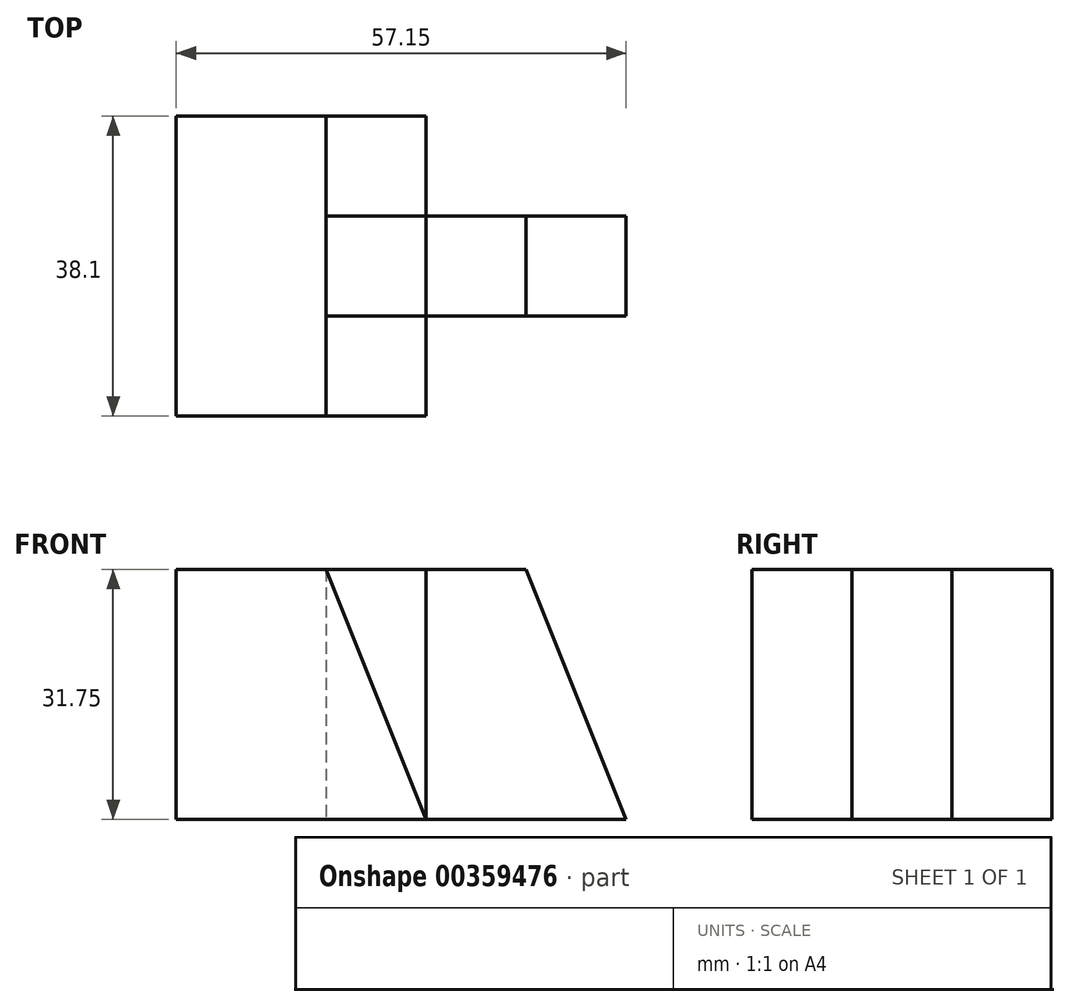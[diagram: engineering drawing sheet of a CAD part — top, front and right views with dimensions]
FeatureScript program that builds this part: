
annotation { "Feature Type Name" : "Feature", "Feature Type Description" : "" }
export const myFeature = defineFeature(function(context is Context, id is Id, definition is map)
    precondition{}
    {
        {
            var Q0;
            Q0=qCreatedBy(makeId("Front.planeOp"),FACE);
            var sketch = newSketch(context, id + "F0", { "sketchPlane" : qUnion([Q0])});
            skLineSegment(sketch, "E0", {"start": v(0, 31.75) * mm, "end": v(0, 0) * mm});
            skLineSegment(sketch, "E1", {"start": v(0, 0) * mm, "end": v(31.75, 0) * mm});
            skLineSegment(sketch, "E2", {"start": v(31.75, 0) * mm, "end": v(31.75, 31.75) * mm});
            skLineSegment(sketch, "E3", {"start": v(31.75, 31.75) * mm, "end": v(0, 31.75) * mm});
            skSolve(sketch);
        }
        {
            var Q0;
            Q0=makeQuery(id+"F0.imprint","IMPRINT",FACE,{"disambiguationData":[TD([[makeQuery(id+"F0.imprint","IMPRINT",EDGE,{"derivedFrom":sQuery(id+"F0.wireOp",EDGE,"E0")}),1.0]])]});
            extrude(context, id + "F1", {"entities" : qUnion([Q0]), "oppositeDirection" : true, "depth" : 38.1 * mm});
        }
        {
            var Q0;
            Q0=qCreatedBy(makeId("Right.planeOp"),FACE);
            var sketch = newSketch(context, id + "F2", { "sketchPlane" : qUnion([Q0])});
            skLineSegment(sketch, "E4", {"start": v(12.7, 31.75) * mm, "end": v(12.7, 0) * mm});
            skLineSegment(sketch, "E5", {"start": v(12.7, 0) * mm, "end": v(25.4, 0) * mm});
            skLineSegment(sketch, "E6", {"start": v(25.4, 0) * mm, "end": v(25.4, 31.75) * mm});
            skLineSegment(sketch, "E7", {"start": v(12.7, 31.75) * mm, "end": v(25.4, 31.75) * mm});
            skSolve(sketch);
        }
        {
            var Q0;
            Q0 = qSketchRegion(id + "F2", true);
            extrude(context, id + "F3", {"entities" : qUnion([Q0]), "operationType" : NewBodyOperationType.ADD, "depth" : 57.15 * mm});
        }
        {
            var Q0;
            Q0=qCreatedBy(makeId("Front.planeOp"),FACE);
            var sketch = newSketch(context, id + "F4", { "sketchPlane" : qUnion([Q0])});
            skLineSegment(sketch, "E8", {"start": v(44.45, 31.75) * mm, "end": v(57.15, 0) * mm});
            skLineSegment(sketch, "E9", {"start": v(57.15, 0) * mm, "end": v(57.15, 31.75) * mm});
            skLineSegment(sketch, "E10", {"start": v(57.15, 31.75) * mm, "end": v(44.45, 31.75) * mm});
            skSolve(sketch);
        }
        {
            var Q0;
            Q0 = qSketchRegion(id + "F4", true);
            extrude(context, id + "F5", {"entities" : qUnion([Q0]), "operationType" : NewBodyOperationType.REMOVE, "oppositeDirection" : true, "depth" : 25.4 * mm});
        }
        {
            var Q0;
            Q0=qCreatedBy(makeId("Front.planeOp"),FACE);
            var sketch = newSketch(context, id + "F6", { "sketchPlane" : qUnion([Q0])});
            skLineSegment(sketch, "E11", {"start": v(19.05, 31.75) * mm, "end": v(31.75, 0) * mm});
            skLineSegment(sketch, "E12", {"start": v(31.75, 0) * mm, "end": v(31.75, 31.75) * mm});
            skLineSegment(sketch, "E13", {"start": v(31.75, 31.75) * mm, "end": v(19.05, 31.75) * mm});
            skSolve(sketch);
        }
        {
            var Q0;
            Q0 = qSketchRegion(id + "F6", true);
            extrude(context, id + "F7", {"entities" : qUnion([Q0]), "operationType" : NewBodyOperationType.REMOVE, "oppositeDirection" : true, "depth" : 12.7 * mm});
        }
        {
            var Q0;
            Q0=qCreatedBy(makeId("Front.planeOp"),FACE);
            var sketch = newSketch(context, id + "F8", { "sketchPlane" : qUnion([Q0])});
            skLineSegment(sketch, "E14", {"start": v(31.75, 0) * mm, "end": v(19.05, 31.75) * mm});
            skLineSegment(sketch, "E15", {"start": v(19.05, 31.75) * mm, "end": v(31.75, 31.75) * mm});
            skLineSegment(sketch, "E16", {"start": v(31.75, 31.75) * mm, "end": v(31.75, 0) * mm});
            skSolve(sketch);
        }
        {
            var Q0;
            Q0 = qSketchRegion(id + "F8", true);
            extrude(context, id + "F9", {"entities" : qUnion([Q0]), "operationType" : NewBodyOperationType.REMOVE, "oppositeDirection" : true, "depth" : 38.1 * mm});
        }
        {
            var Q0;
            Q0=qCreatedBy(makeId("Top.planeOp"),FACE);
            var sketch = newSketch(context, id + "F10", { "sketchPlane" : qUnion([Q0])});
            skLineSegment(sketch, "E17", {"start": v(31.75, 25.4) * mm, "end": v(19.05, 25.4) * mm});
            skLineSegment(sketch, "E18", {"start": v(19.05, 25.4) * mm, "end": v(19.05, 12.7) * mm});
            skLineSegment(sketch, "E19", {"start": v(19.05, 12.7) * mm, "end": v(31.75, 12.7) * mm});
            skLineSegment(sketch, "E20", {"start": v(31.75, 12.7) * mm, "end": v(31.75, 25.4) * mm});
            skSolve(sketch);
        }
        {
            var Q0;
            Q0 = qSketchRegion(id + "F10", true);
            extrude(context, id + "F11", {"entities" : qUnion([Q0]), "depth" : 31.75 * mm});
        }
    });
